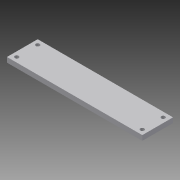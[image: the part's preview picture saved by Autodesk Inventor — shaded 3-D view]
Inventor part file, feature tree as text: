
AUTODESK INVENTOR PART (.ipt)
format: ipt  version: 2013 (Build 170138000, 138)  size: 80,384 bytes
history: native  units: mm
features: hole x4, extrude x1, sketch x1
ambient origin geometry x8: Origin, YZ Plane, XZ Plane, XY Plane, X Axis, Y Axis, Z Axis, Center Point
bodies: Volumenkörper1 (feature_tree)
feature tree (6):
  extrude  "Extrusion1"  Depth=25.0mm
  hole  "Bohrung1"  [1 undecoded]
  hole  "Bohrung2"  [1 undecoded]
  hole  "Bohrung3"  [1 undecoded]
  hole  "Bohrung4"  [1 undecoded]
  sketch  "Skizze1"  dims[d0=110.0mm d1=25.0mm d2=4.0mm d3=0.0mm d4=4.0mm d5=4.0mm d6=3.2mm d7=6.0mm d8=4.0mm d9=2.0mm d10=90.0deg d11=8.0mm d12=20.594885mm d13=4.0mm d14=4.0mm d15=3.2mm d16=6.0mm d17=4.0mm d18=2.0mm d19=90.0deg d20=8.0mm d21=20.594885mm d22=4.0mm d23=4.0mm d24=3.2mm d25=6.0mm d26=4.0mm d27=2.0mm d28=90.0deg d29=8.0mm d30=20.594885mm d31=4.0mm d32=4.0mm d33=3.2mm d34=6.0mm d35=4.0mm d36=2.0mm d37=90.0deg d38=8.0mm d39=20.594885mm]
note: 4 required parameter values undecoded (feature->parameter linkage not recoverable at this tier; creation-order binding heuristic only, values carry confidence <= 0.55)
